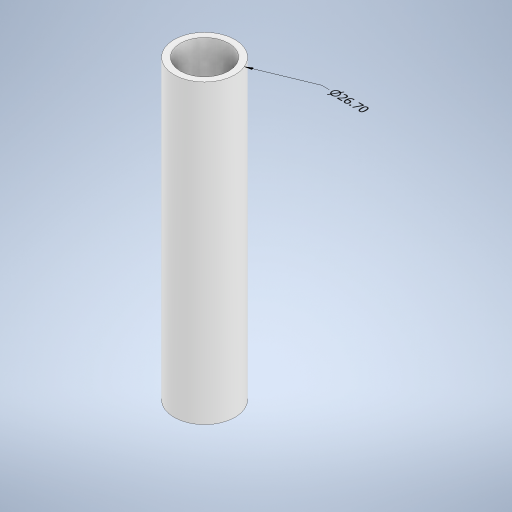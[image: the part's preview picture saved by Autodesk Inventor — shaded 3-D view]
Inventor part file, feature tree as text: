
AUTODESK INVENTOR PART (.ipt)
format: ipt  version: 2023.1 (Build 271208000, 208)  size: 241,664 bytes
history: native  units: mm
features: other x2, revolve x1, sketch x1
ambient origin geometry x8: Origin, YZ Plane, XZ Plane, XY Plane, X Axis, Y Axis, Z Axis, Center Point
bodies: Solid1 (feature_tree)
feature tree (4):
  other  "Annotations"
  revolve  "Revolution1"  [1 undecoded]
  sketch  "Sketch1"  dims[d6=360.0deg d9=21.2mm d10=26.7mm d11=130.0mm d12=37.202058mm d13=26.7mm]
  other  "Diameter Dimension 1"
note: 1 required parameter value undecoded (feature->parameter linkage not recoverable at this tier; creation-order binding heuristic only, values carry confidence <= 0.55)
